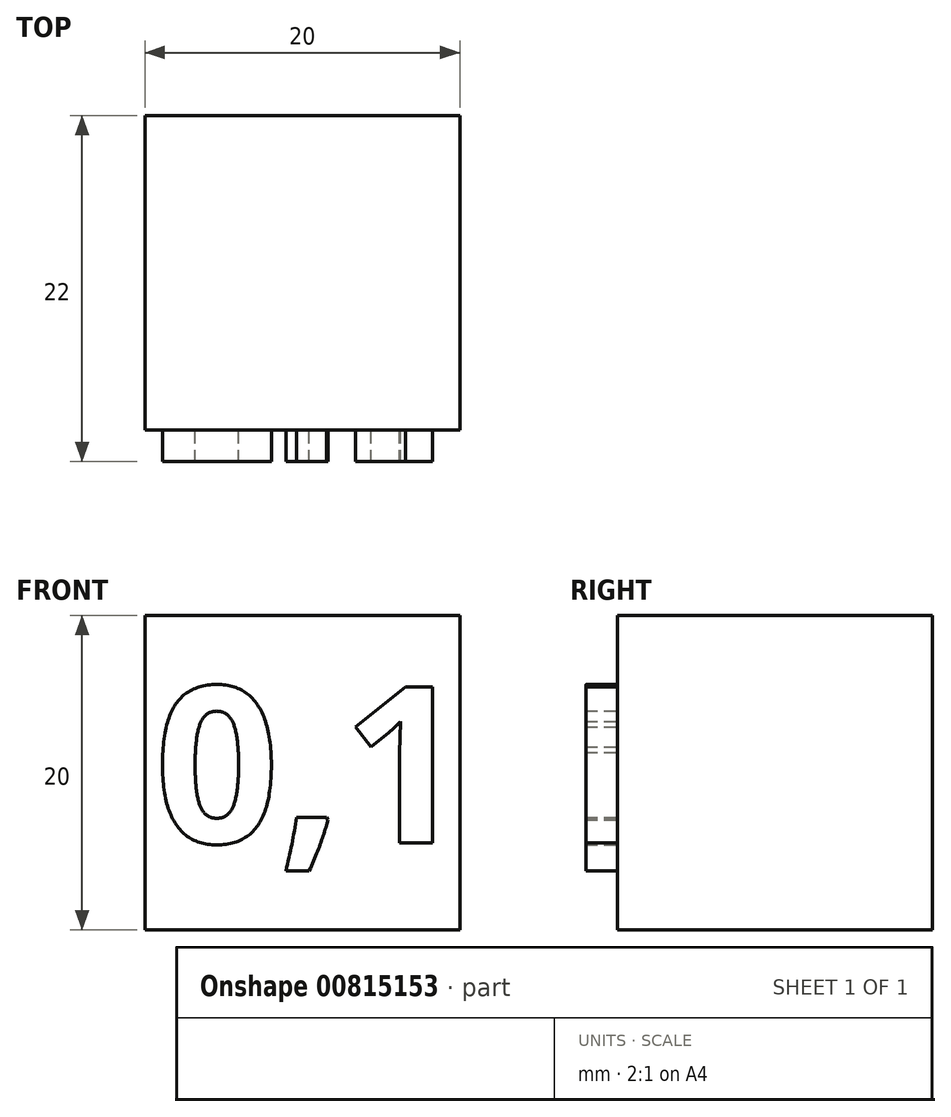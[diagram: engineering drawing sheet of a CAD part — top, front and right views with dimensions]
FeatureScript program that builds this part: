
annotation { "Feature Type Name" : "Feature", "Feature Type Description" : "" }
export const myFeature = defineFeature(function(context is Context, id is Id, definition is map)
    precondition{}
    {
        {
            var Q0;
            Q0=qCreatedBy(makeId("Front.planeOp"),FACE);
            var sketch = newSketch(context, id + "F0", { "sketchPlane" : qUnion([Q0])});
            skLineSegment(sketch, "E0.bottom", {"start": v(0, 0) * mm, "end": v(-20, 0) * mm});
            skLineSegment(sketch, "E0.top", {"start": v(0, 20) * mm, "end": v(-20, 20) * mm});
            skLineSegment(sketch, "E0.left", {"start": v(0, 0) * mm, "end": v(0, 20) * mm});
            skLineSegment(sketch, "E0.right", {"start": v(-20, 0) * mm, "end": v(-20, 20) * mm});
            skSolve(sketch);
        }
        {
            var Q0;
            Q0=makeQuery(id+"F0.imprint","IMPRINT",FACE,{"disambiguationData":[TD([[makeQuery(id+"F0.imprint","IMPRINT",EDGE,{"derivedFrom":sQuery(id+"F0.wireOp",EDGE,"E0.bottom")}),-1.0]])]});
            extrude(context, id + "F1", {"entities" : qUnion([Q0]), "depth" : 20 * mm, "offsetDistance" : 25 * mm});
        }
        {
            var Q0;
            Q0=makeQuery(id+"F1.opExtrude","CAP_FACE",FACE,{"disambiguationData":[OSD([sQuery(id+"F0.wireOp",EDGE,"E0.bottom"),sQuery(id+"F0.wireOp",EDGE,"E0.top"),sQuery(id+"F0.wireOp",EDGE,"E0.left"),sQuery(id+"F0.wireOp",EDGE,"E0.right")])],"isStart":false});
            var sketch = newSketch(context, id + "F2", { "sketchPlane" : qUnion([Q0])});
            skText(sketch, "E1", { "text": "0,1", "fontName": "OpenSans-Bold.ttf"});
            const initialGuessF2  = {"E1": [-0.01939, 0.00555, 1, 0, 0.00998]};
            skSetInitialGuess(sketch, initialGuessF2);
            skSolve(sketch);
        }
        {
            var Q0;
            Q0=makeQuery(id+"F2.imprint","IMPRINT",FACE,{"disambiguationData":[TD([[makeQuery(id+"F2.imprint","IMPRINT",EDGE,{"derivedFrom":sQuery(id+"F2.wireOp",EDGE,"E1.sketch_text.stroke-0")}),-1.0]])]});
            var Q1;
            Q1=makeQuery(id+"F2.imprint","IMPRINT",FACE,{"disambiguationData":[TD([[makeQuery(id+"F2.imprint","IMPRINT",EDGE,{"derivedFrom":sQuery(id+"F2.wireOp",EDGE,"E1.sketch_text.stroke-16")}),-1.0]])]});
            var Q2;
            Q2=makeQuery(id+"F2.imprint","IMPRINT",FACE,{"disambiguationData":[TD([[makeQuery(id+"F2.imprint","IMPRINT",EDGE,{"derivedFrom":sQuery(id+"F2.wireOp",EDGE,"E1.sketch_text.stroke-21")}),-1.0]])]});
            extrude(context, id + "F3", {"entities" : qUnion([Q0, Q1, Q2]), "operationType" : NewBodyOperationType.ADD, "depth" : 2 * mm, "offsetDistance" : 25 * mm});
        }
    });
